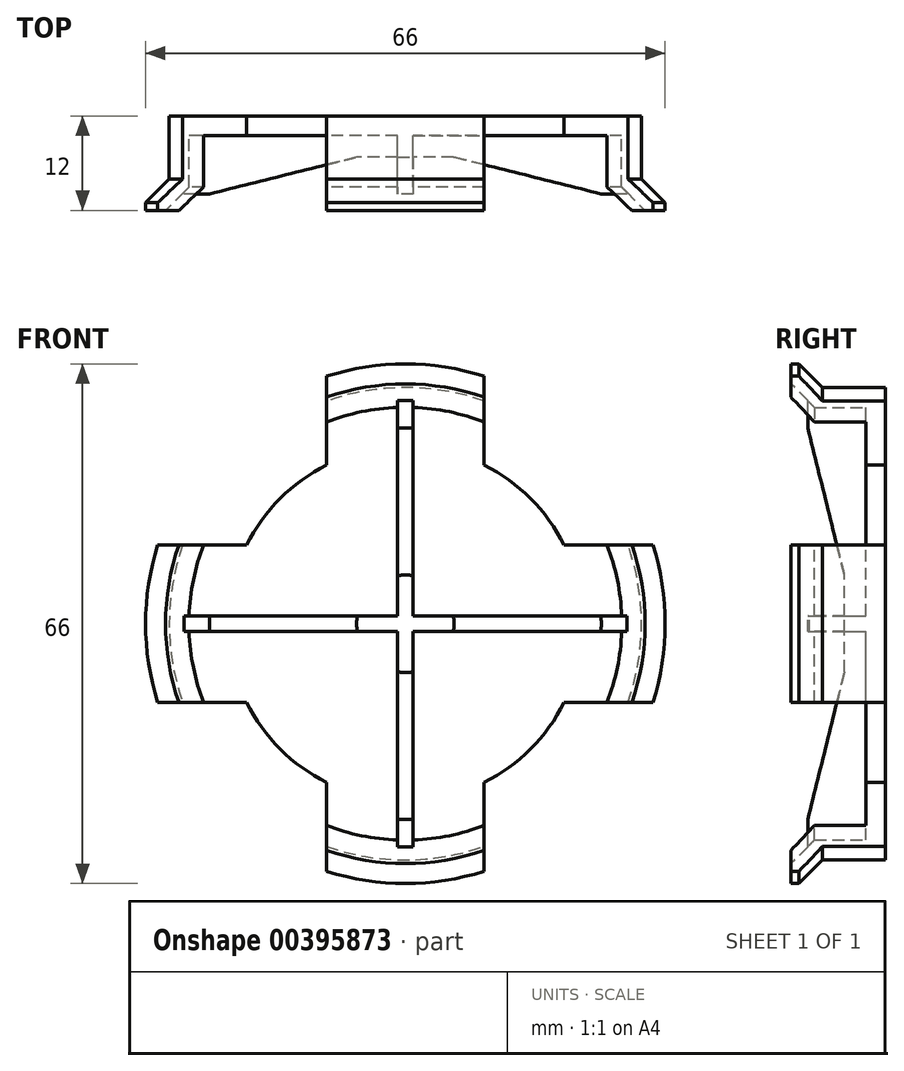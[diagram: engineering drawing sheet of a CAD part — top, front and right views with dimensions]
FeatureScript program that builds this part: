
annotation { "Feature Type Name" : "Feature", "Feature Type Description" : "" }
export const myFeature = defineFeature(function(context is Context, id is Id, definition is map)
    precondition{}
    {
        {
            var Q0;
            Q0=qCreatedBy(makeId("Front.planeOp"),FACE);
            var sketch = newSketch(context, id + "F0", { "sketchPlane" : qUnion([Q0])});
            skCircle(sketch, "E0", {"center": v(0, 0) * mm, "radius": 30 * mm});
            skSolve(sketch);
        }
        {
            var Q0;
            Q0 = qSketchRegion(id + "F0", true);
            extrude(context, id + "F1", {"entities" : qUnion([Q0]), "depth" : 8 * mm});
        }
        {
            var Q0;
            Q0=makeQuery(id+"F1.opExtrude","CAP_FACE",FACE,{"disambiguationData":[OSD([sQuery(id+"F0.wireOp",EDGE,"E0")])],"isStart":false});
            var sketch = newSketch(context, id + "F2", { "sketchPlane" : qUnion([Q0])});
            skCircle(sketch, "E1", {"center": v(0, 0) * mm, "radius": 33 * mm});
            skSolve(sketch);
        }
        {
            var Q0;
            Q0 = qSketchRegion(id + "F2", true);
            extrude(context, id + "F3", {"entities" : qUnion([Q0]), "operationType" : NewBodyOperationType.ADD, "depth" : 4 * mm});
        }
        {
            var Q0;
            Q0=makeQuery(id+"F3.opExtrude","CAP_EDGE",EDGE,{"disambiguationData":[OSD([sQuery(id+"F2.wireOp",EDGE,"E1")])],"isStart":true});
            chamfer(context, id + "F4", {"entities" : qUnion([Q0]), "width" : 3 * mm, "tangentPropagation" : true});
        }
        {
            var Q0;
            Q0=makeQuery(id+"F3.opExtrude","CAP_FACE",FACE,{"disambiguationData":[OSD([sQuery(id+"F2.wireOp",EDGE,"E1")])],"isStart":false});
            shell(context, id + "F5", {"entities" : qUnion([Q0]), "thickness" : 2.5 * mm});
        }
        {
            var Q0;
            Q0=makeQuery(id+"F1.opExtrude","CAP_FACE",FACE,{"disambiguationData":[OSD([sQuery(id+"F0.wireOp",EDGE,"E0")])],"isStart":true});
            var sketch = newSketch(context, id + "F6", { "sketchPlane" : qUnion([Q0])});
            skArc(sketch, "E2", {"start": v(-10, 20.16) * mm, "mid": v(-15.9, 15.9) * mm, "end": v(-20.16, 10) * mm});
            skLineSegment(sketch, "E3.bottom", {"start": v(10, 86.75) * mm, "end": v(-10, 86.75) * mm});
            skPoint(sketch, "E3.middle", {"position": v(0, 22.5) * mm});
            skLineSegment(sketch, "E4.bottom", {"start": v(42.4, -10) * mm, "end": v(20.16, -10) * mm});
            skLineSegment(sketch, "E4.top", {"start": v(42.4, 10) * mm, "end": v(20.16, 10) * mm});
            skLineSegment(sketch, "E5.left", {"start": v(10, 42.54) * mm, "end": v(10, 20.16) * mm});
            skLineSegment(sketch, "E5.right", {"start": v(-10, 42.54) * mm, "end": v(-10, 20.16) * mm});
            skLineSegment(sketch, "E6", {"start": v(-42.4, 10) * mm, "end": v(-10, 42.54) * mm});
            skLineSegment(sketch, "E7", {"start": v(10, 42.54) * mm, "end": v(42.4, 10) * mm});
            skLineSegment(sketch, "E8", {"start": v(42.4, -10) * mm, "end": v(10, -42.54) * mm});
            skLineSegment(sketch, "E9", {"start": v(-10, -42.54) * mm, "end": v(-42.4, -10) * mm});
            skLineSegment(sketch, "E10.trimOffspring", {"start": v(10, -20.16) * mm, "end": v(10, -42.54) * mm});
            skLineSegment(sketch, "E11.trimOffspring", {"start": v(-20.16, 10) * mm, "end": v(-42.4, 10) * mm});
            skLineSegment(sketch, "E12.trimOffspring", {"start": v(-20.16, -10) * mm, "end": v(-42.4, -10) * mm});
            skLineSegment(sketch, "E13.trimOffspring", {"start": v(-10, -20.16) * mm, "end": v(-10, -42.54) * mm});
            skArc(sketch, "E14.trimOffspring", {"start": v(20.16, 10) * mm, "mid": v(15.9, 15.9) * mm, "end": v(10, 20.16) * mm});
            skArc(sketch, "E15.trimOffspring", {"start": v(10, -20.16) * mm, "mid": v(15.9, -15.9) * mm, "end": v(20.16, -10) * mm});
            skArc(sketch, "E16.trimOffspring", {"start": v(-20.16, -10) * mm, "mid": v(-15.9, -15.9) * mm, "end": v(-10, -20.16) * mm});
            skSolve(sketch);
        }
        {
            var Q0;
            Q0 = qSketchRegion(id + "F6", true);
            extrude(context, id + "F7", {"entities" : qUnion([Q0]), "operationType" : NewBodyOperationType.REMOVE, "oppositeDirection" : true, "depth" : 25.4 * mm});
        }
        {
            var Q0;
            {var subQ0=sQuery(id+"F0.wireOp",EDGE,"E0");Q0=makeQuery(id+"F5.opShell","OFFSET_FACE",FACE,{"disambiguationData":[OSD([subQ0]),TDD([makeQuery(id+"F1.opExtrude","CAP_FACE",FACE,{"disambiguationData":[OSD([subQ0])],"isStart":true})])]});}
            var sketch = newSketch(context, id + "F8", { "sketchPlane" : qUnion([Q0])});
            skLineSegment(sketch, "E17.bottom", {"start": v(1, -28.41) * mm, "end": v(-1, -28.41) * mm});
            skLineSegment(sketch, "E17.top", {"start": v(1, 28.41) * mm, "end": v(-1, 28.41) * mm});
            skLineSegment(sketch, "E17.left", {"start": v(1, -28.41) * mm, "end": v(1, 28.41) * mm});
            skLineSegment(sketch, "E17.right", {"start": v(-1, -28.41) * mm, "end": v(-1, 28.41) * mm});
            skPoint(sketch, "E17.middle", {"position": v(0, 0) * mm});
            skLineSegment(sketch, "E18.bottom", {"start": v(28.13, -1) * mm, "end": v(-28.13, -1) * mm});
            skLineSegment(sketch, "E18.top", {"start": v(28.13, 1) * mm, "end": v(-28.13, 1) * mm});
            skLineSegment(sketch, "E18.left", {"start": v(28.13, -1) * mm, "end": v(28.13, 1) * mm});
            skLineSegment(sketch, "E18.right", {"start": v(-28.13, -1) * mm, "end": v(-28.13, 1) * mm});
            skSolve(sketch);
        }
        {
            var Q0;
            Q0 = qSketchRegion(id + "F8", true);
            extrude(context, id + "F9", {"entities" : qUnion([Q0]), "operationType" : NewBodyOperationType.ADD, "depth" : 7.4 * mm});
        }
        {
            var Q0;
            Q0=makeQuery(id+"F9.opExtrude","CAP_FACE",FACE,{"disambiguationData":[OSD([sQuery(id+"F8.wireOp",EDGE,"E17.bottom"),sQuery(id+"F8.wireOp",EDGE,"E17.top"),sQuery(id+"F8.wireOp",EDGE,"E17.left"),sQuery(id+"F8.wireOp",EDGE,"E17.right"),sQuery(id+"F8.wireOp",EDGE,"E18.bottom"),sQuery(id+"F8.wireOp",EDGE,"E18.top"),sQuery(id+"F8.wireOp",EDGE,"E18.left"),sQuery(id+"F8.wireOp",EDGE,"E18.right")])],"isStart":false});
            var sketch = newSketch(context, id + "F10", { "sketchPlane" : qUnion([Q0])});
            skCircle(sketch, "E19", {"center": v(0, 0) * mm, "radius": 26.2 * mm});
            skSolve(sketch);
        }
        {
            var Q0;
            Q0 = qSketchRegion(id + "F10", true);
            extrude(context, id + "F11", {"entities" : qUnion([Q0]), "operationType" : NewBodyOperationType.REMOVE, "oppositeDirection" : true, "depth" : 4.67 * mm});
        }
        {
            var Q0;
            {var subQ0=sQuery(id+"F8.wireOp",EDGE,"E18.right");var subQ1=sQuery(id+"F8.wireOp",EDGE,"E18.bottom");var subQ5=sQuery(id+"F8.wireOp",EDGE,"E17.right");var subQ6=sQuery(id+"F10.wireOp",EDGE,"E19");Q0=makeQuery(id+"F11.boolean.opBoolean","COPY",EDGE,{"disambiguationData":[TD([makeQuery(id+"F9.opExtrude","SWEPT_FACE",FACE,{"disambiguationData":[OSD([subQ1]),TDD([makeQuery(id+"F8.imprint","IMPRINT",EDGE,{"disambiguationData":[TD([[makeQuery(id+"F8.imprint","INTERSECT",VERTEX,{"derivedFrom":[subQ5,subQ1]}),-1.0]])],"derivedFrom":subQ1}),makeQuery(id+"F8.imprint","IMPRINT",EDGE,{"disambiguationData":[TD([[makeQuery(id+"F8.imprint","INTERSECT",VERTEX,{"derivedFrom":[subQ1,subQ0]}),1.0]])],"derivedFrom":subQ1})])]})])],"derivedFrom":makeQuery(id+"F11.opExtrude","CAP_EDGE",EDGE,{"disambiguationData":[OSD([subQ6])],"isStart":false})});}
            var Q1;
            {var subQ0=sQuery(id+"F8.wireOp",EDGE,"E17.left");var subQ1=sQuery(id+"F8.wireOp",EDGE,"E17.top");var subQ5=sQuery(id+"F8.wireOp",EDGE,"E18.top");var subQ8=sQuery(id+"F10.wireOp",EDGE,"E19");Q1=makeQuery(id+"F11.boolean.opBoolean","COPY",EDGE,{"disambiguationData":[TD([makeQuery(id+"F9.opExtrude","SWEPT_FACE",FACE,{"disambiguationData":[OSD([subQ0]),TDD([makeQuery(id+"F8.imprint","IMPRINT",EDGE,{"disambiguationData":[TD([[makeQuery(id+"F8.imprint","INTERSECT",VERTEX,{"derivedFrom":[subQ0,subQ5]}),-1.0]])],"derivedFrom":subQ0}),makeQuery(id+"F8.imprint","IMPRINT",EDGE,{"disambiguationData":[TD([[makeQuery(id+"F8.imprint","INTERSECT",VERTEX,{"derivedFrom":[subQ1,subQ0]}),1.0]])],"derivedFrom":subQ0})])]})])],"derivedFrom":makeQuery(id+"F11.opExtrude","CAP_EDGE",EDGE,{"disambiguationData":[OSD([subQ8])],"isStart":false})});}
            var Q2;
            {var subQ0=sQuery(id+"F8.wireOp",EDGE,"E18.bottom");var subQ1=sQuery(id+"F8.wireOp",EDGE,"E17.left");var subQ5=sQuery(id+"F8.wireOp",EDGE,"E18.left");var subQ8=sQuery(id+"F10.wireOp",EDGE,"E19");Q2=makeQuery(id+"F11.boolean.opBoolean","COPY",EDGE,{"disambiguationData":[TD([makeQuery(id+"F9.opExtrude","SWEPT_FACE",FACE,{"disambiguationData":[OSD([subQ0]),TDD([makeQuery(id+"F8.imprint","IMPRINT",EDGE,{"disambiguationData":[TD([[makeQuery(id+"F8.imprint","INTERSECT",VERTEX,{"derivedFrom":[subQ0,subQ5]}),-1.0]])],"derivedFrom":subQ0}),makeQuery(id+"F8.imprint","IMPRINT",EDGE,{"disambiguationData":[TD([[makeQuery(id+"F8.imprint","INTERSECT",VERTEX,{"derivedFrom":[subQ1,subQ0]}),1.0]])],"derivedFrom":subQ0})])]})])],"derivedFrom":makeQuery(id+"F11.opExtrude","CAP_EDGE",EDGE,{"disambiguationData":[OSD([subQ8])],"isStart":false})});}
            var Q3;
            {var subQ0=sQuery(id+"F8.wireOp",EDGE,"E18.bottom");var subQ1=sQuery(id+"F8.wireOp",EDGE,"E17.left");var subQ5=sQuery(id+"F8.wireOp",EDGE,"E17.bottom");var subQ6=sQuery(id+"F10.wireOp",EDGE,"E19");Q3=makeQuery(id+"F11.boolean.opBoolean","COPY",EDGE,{"disambiguationData":[TD([makeQuery(id+"F9.opExtrude","SWEPT_FACE",FACE,{"disambiguationData":[OSD([subQ1]),TDD([makeQuery(id+"F8.imprint","IMPRINT",EDGE,{"disambiguationData":[TD([[makeQuery(id+"F8.imprint","INTERSECT",VERTEX,{"derivedFrom":[subQ5,subQ1]}),-1.0]])],"derivedFrom":subQ1}),makeQuery(id+"F8.imprint","IMPRINT",EDGE,{"disambiguationData":[TD([[makeQuery(id+"F8.imprint","INTERSECT",VERTEX,{"derivedFrom":[subQ1,subQ0]}),1.0]])],"derivedFrom":subQ1})])]})])],"derivedFrom":makeQuery(id+"F11.opExtrude","CAP_EDGE",EDGE,{"disambiguationData":[OSD([subQ6])],"isStart":false})});}
            chamfer(context, id + "F12", {"entities" : qUnion([Q0, Q1, Q2, Q3]), "chamferType" : ChamferType.TWO_OFFSETS, "width1" : 20 * mm, "oppositeDirection" : false, "width2" : 5 * mm, "tangentPropagation" : true});
        }
    });
